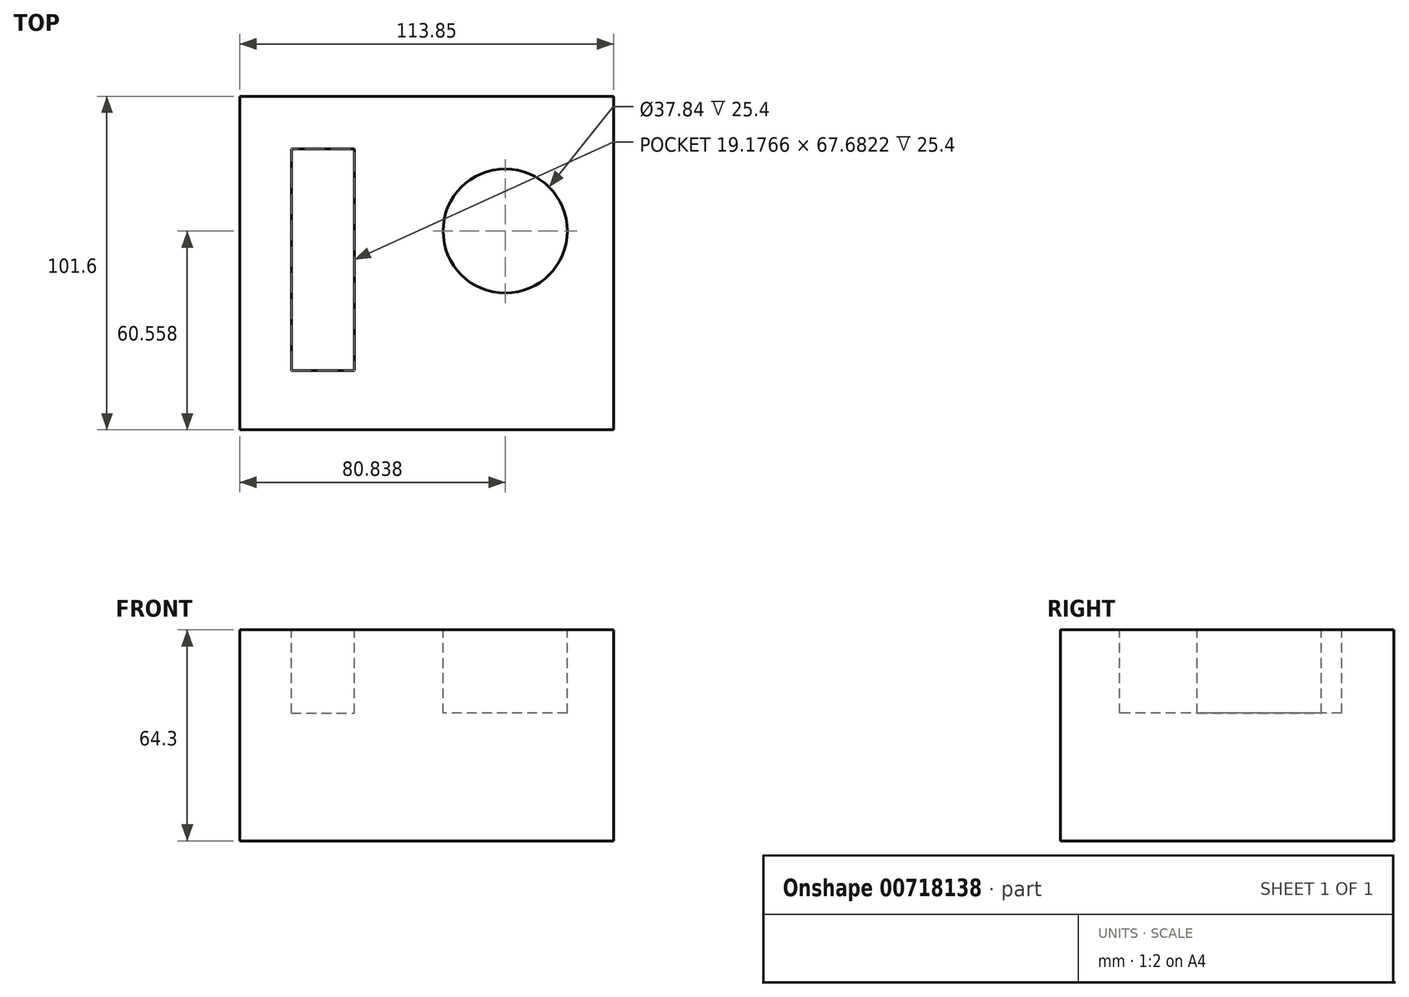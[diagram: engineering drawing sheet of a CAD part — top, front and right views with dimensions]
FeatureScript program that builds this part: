
annotation { "Feature Type Name" : "Feature", "Feature Type Description" : "" }
export const myFeature = defineFeature(function(context is Context, id is Id, definition is map)
    precondition{}
    {
        {
            var Q0;
            Q0=qCreatedBy(makeId("Front.planeOp"),FACE);
            var sketch = newSketch(context, id + "F0", { "sketchPlane" : qUnion([Q0])});
            skLineSegment(sketch, "E0.bottom", {"start": v(-53.06, 40) * mm, "end": v(60.8, 40) * mm});
            skLineSegment(sketch, "E0.top", {"start": v(-53.06, -24.3) * mm, "end": v(60.8, -24.3) * mm});
            skLineSegment(sketch, "E0.left", {"start": v(-53.06, 40) * mm, "end": v(-53.06, -24.3) * mm});
            skLineSegment(sketch, "E0.right", {"start": v(60.8, 40) * mm, "end": v(60.8, -24.3) * mm});
            skSolve(sketch);
        }
        {
            var Q0;
            Q0=makeQuery(id+"F0.imprint","IMPRINT",FACE,{"disambiguationData":[TD([[makeQuery(id+"F0.imprint","IMPRINT",EDGE,{"derivedFrom":sQuery(id+"F0.wireOp",EDGE,"E0.bottom")}),-1.0]])]});
            extrude(context, id + "F1", {"entities" : qUnion([Q0]), "depth" : 101.6 * mm, "offsetDistance" : 25.4 * mm});
        }
        {
            var Q0;
            Q0=makeQuery(id+"F1.opExtrude","SWEPT_FACE",FACE,{"disambiguationData":[OSD([sQuery(id+"F0.wireOp",EDGE,"E0.bottom")])]});
            var sketch = newSketch(context, id + "F2", { "sketchPlane" : qUnion([Q0])});
            skLineSegment(sketch, "E1.bottom", {"start": v(-37.37, -15.94) * mm, "end": v(-18.19, -15.94) * mm});
            skLineSegment(sketch, "E1.top", {"start": v(-37.37, -83.63) * mm, "end": v(-18.19, -83.63) * mm});
            skLineSegment(sketch, "E1.left", {"start": v(-37.37, -15.94) * mm, "end": v(-37.37, -83.63) * mm});
            skLineSegment(sketch, "E1.right", {"start": v(-18.19, -15.94) * mm, "end": v(-18.19, -83.63) * mm});
            skCircle(sketch, "E2", {"center": v(27.78, -41.04) * mm, "radius": 18.92 * mm});
            skSolve(sketch);
        }
        {
            var Q0;
            Q0=makeQuery(id+"F2.imprint","IMPRINT",FACE,{"disambiguationData":[TD([[makeQuery(id+"F2.imprint","IMPRINT",EDGE,{"derivedFrom":sQuery(id+"F2.wireOp",EDGE,"E1.bottom")}),-1.0]])]});
            var Q1;
            Q1=makeQuery(id+"F2.imprint","IMPRINT",FACE,{"disambiguationData":[TD([[makeQuery(id+"F2.imprint","IMPRINT",EDGE,{"derivedFrom":sQuery(id+"F2.wireOp",EDGE,"E2")}),1.0]])]});
            extrude(context, id + "F3", {"entities" : qUnion([Q0, Q1]), "operationType" : NewBodyOperationType.REMOVE, "oppositeDirection" : true, "depth" : 25.4 * mm, "offsetDistance" : 25.4 * mm});
        }
    });
